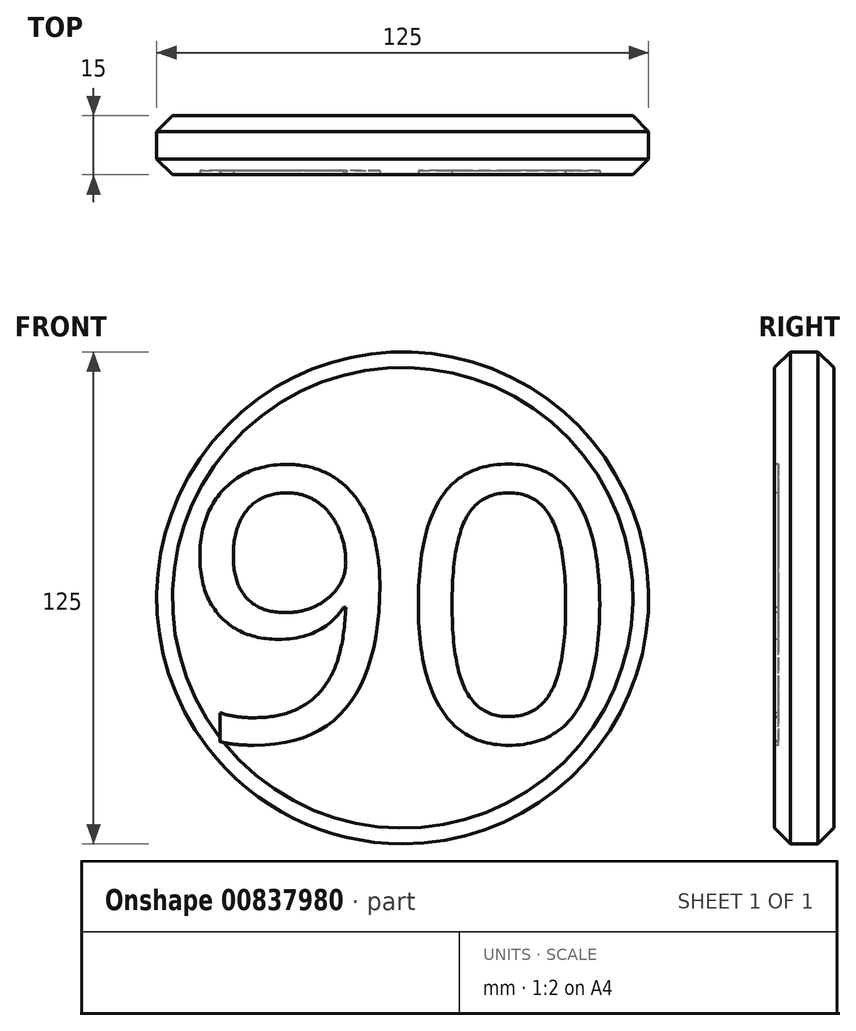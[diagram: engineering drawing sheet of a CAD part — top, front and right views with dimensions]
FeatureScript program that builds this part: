
annotation { "Feature Type Name" : "Feature", "Feature Type Description" : "" }
export const myFeature = defineFeature(function(context is Context, id is Id, definition is map)
    precondition{}
    {
        {
            var Q0;
            Q0=qCreatedBy(makeId("Front.planeOp"),FACE);
            var sketch = newSketch(context, id + "F0", { "sketchPlane" : qUnion([Q0])});
            skCircle(sketch, "E0", {"center": v(0, 0) * mm, "radius": 62.5 * mm});
            skSolve(sketch);
        }
        {
            var Q0;
            Q0 = qSketchRegion(id + "F0", true);
            extrude(context, id + "F1", {"entities" : qUnion([Q0]), "depth" : 15 * mm, "offsetDistance" : 25 * mm});
        }
        {
            var Q0;
            Q0=makeQuery(id+"F1.opExtrude","CAP_EDGE",EDGE,{"disambiguationData":[OSD([sQuery(id+"F0.wireOp",EDGE,"E0")])],"isStart":false});
            var Q1;
            Q1=makeQuery(id+"F1.opExtrude","CAP_EDGE",EDGE,{"disambiguationData":[OSD([sQuery(id+"F0.wireOp",EDGE,"E0")])],"isStart":true});
            chamfer(context, id + "F2", {"entities" : qUnion([Q0, Q1]), "width" : 4 * mm, "tangentPropagation" : true});
        }
        {
            var Q0;
            Q0=makeQuery(id+"F1.opExtrude","CAP_FACE",FACE,{"disambiguationData":[OSD([sQuery(id+"F0.wireOp",EDGE,"E0")])],"isStart":false});
            var sketch = newSketch(context, id + "F3", { "sketchPlane" : qUnion([Q0])});
            skText(sketch, "E1", { "text": "90", "fontName": "NotoSans-Regular.ttf"});
            const initialGuessF3  = {"E1": [-0.05637, -0.0365, 1, 0, 0.07]};
            skSetInitialGuess(sketch, initialGuessF3);
            skSolve(sketch);
        }
        {
            var Q0;
            Q0 = qSketchRegion(id + "F3", true);
            extrude(context, id + "F4", {"entities" : qUnion([Q0]), "operationType" : NewBodyOperationType.REMOVE, "oppositeDirection" : true, "depth" : 1 * mm, "offsetDistance" : 25 * mm});
        }
    });
